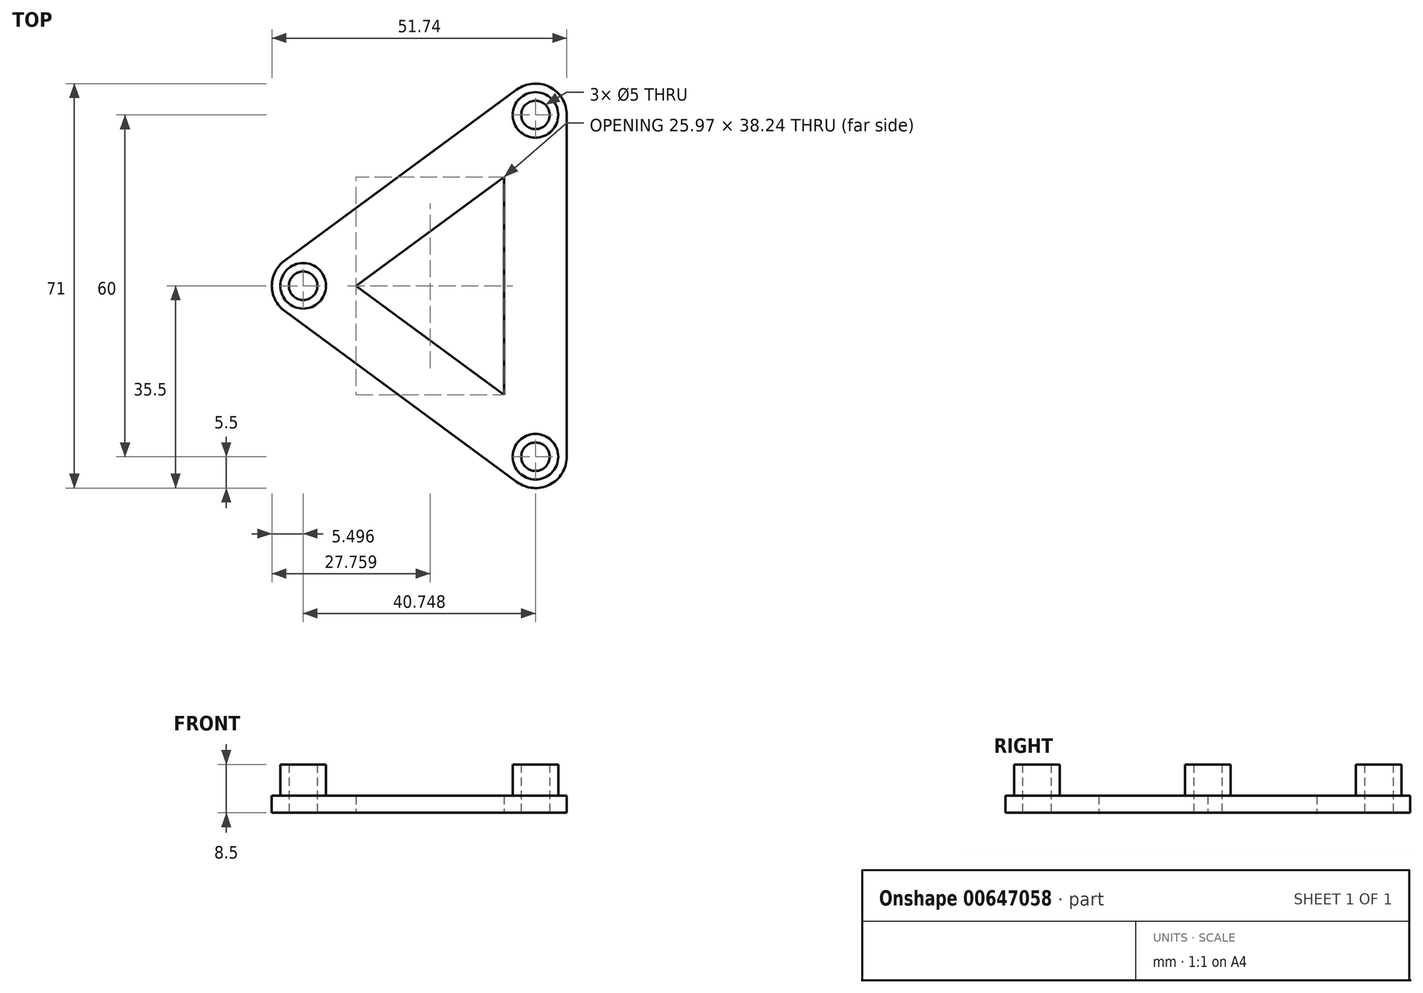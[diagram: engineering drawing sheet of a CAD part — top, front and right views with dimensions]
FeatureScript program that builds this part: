
annotation { "Feature Type Name" : "Feature", "Feature Type Description" : "" }
export const myFeature = defineFeature(function(context is Context, id is Id, definition is map)
    precondition{}
    {
        {
            var Q0;
            Q0=qCreatedBy(makeId("Top.planeOp"),FACE);
            var sketch = newSketch(context, id + "F0", { "sketchPlane" : qUnion([Q0])});
            skCircle(sketch, "E0", {"center": v(-17.31, 0) * mm, "radius": 2.5 * mm});
            skCircle(sketch, "E1", {"center": v(-17.31, 0) * mm, "radius": 5.5 * mm});
            skCircle(sketch, "E2", {"center": v(23.43, 30) * mm, "radius": 2.5 * mm});
            skCircle(sketch, "E3", {"center": v(23.43, 30) * mm, "radius": 5.5 * mm});
            skCircle(sketch, "E4", {"center": v(23.43, -30) * mm, "radius": 2.5 * mm});
            skCircle(sketch, "E5", {"center": v(23.43, -30) * mm, "radius": 5.5 * mm});
            skLineSegment(sketch, "E6", {"start": v(-17.31, 0) * mm, "end": v(23.43, 30) * mm, "construction": true});
            skLineSegment(sketch, "E7", {"start": v(-17.31, 0) * mm, "end": v(23.43, -30) * mm, "construction": true});
            skLineSegment(sketch, "E8", {"start": v(23.43, 30) * mm, "end": v(23.43, -30) * mm, "construction": true});
            skCircle(sketch, "E9", {"center": v(-17.31, 0) * mm, "radius": 4 * mm});
            skCircle(sketch, "E10", {"center": v(23.43, 30) * mm, "radius": 4 * mm});
            skCircle(sketch, "E11", {"center": v(23.43, -30) * mm, "radius": 4 * mm});
            skLineSegment(sketch, "E12.0", {"start": v(-8.04, 0) * mm, "end": v(17.93, 19.12) * mm});
            skLineSegment(sketch, "E12.1", {"start": v(-8.04, 0) * mm, "end": v(17.93, -19.12) * mm});
            skLineSegment(sketch, "E12.2", {"start": v(17.93, 19.12) * mm, "end": v(17.93, -19.12) * mm});
            skLineSegment(sketch, "E13.0", {"start": v(-20.57, 4.43) * mm, "end": v(20.17, 34.43) * mm});
            skLineSegment(sketch, "E13.1", {"start": v(-20.57, -4.43) * mm, "end": v(20.17, -34.43) * mm});
            skLineSegment(sketch, "E13.2", {"start": v(28.93, 30) * mm, "end": v(28.93, -30) * mm});
            skLineSegment(sketch, "E14", {"start": v(3.06, 15) * mm, "end": v(3.06, -15) * mm, "construction": true});
            skSolve(sketch);
        }
        {
            var Q0;
            Q0=makeQuery(id+"F0.imprint","IMPRINT",FACE,{"disambiguationData":[TD([[makeQuery(id+"F0.imprint","IMPRINT",EDGE,{"derivedFrom":sQuery(id+"F0.wireOp",EDGE,"E2")}),-1.0]])]});
            var Q1;
            {var subQ0=sQuery(id+"F0.wireOp",EDGE,"4292a800-b917-446e-8acb-4b11a4841fbd.0");var subQ1=sQuery(id+"F0.wireOp",EDGE,"E3");var subQ2=makeQuery(id+"F0.imprint","INTERSECT",VERTEX,{"derivedFrom":[subQ1,subQ0]});Q1=makeQuery(id+"F0.imprint","IMPRINT",FACE,{"disambiguationData":[TD([[makeQuery(id+"F0.imprint","IMPRINT",EDGE,{"disambiguationData":[TD([[subQ2,1.0]])],"derivedFrom":subQ1}),-1.0]])]});}
            var Q2;
            {var subQ0=sQuery(id+"F0.wireOp",EDGE,"b792d51c-0fe7-4bc2-b237-ce6525926208.0");Q2=makeQuery(id+"F0.imprint","IMPRINT",FACE,{"disambiguationData":[TD([[makeQuery(id+"F0.imprint","IMPRINT",EDGE,{"derivedFrom":subQ0}),-1.0]])]});}
            var Q3;
            Q3=makeQuery(id+"F0.imprint","IMPRINT",FACE,{"disambiguationData":[TD([[makeQuery(id+"F0.imprint","IMPRINT",EDGE,{"derivedFrom":sQuery(id+"F0.wireOp",EDGE,"E0")}),-1.0]])]});
            var Q4;
            {var subQ5=sQuery(id+"F0.wireOp",EDGE,"534e31a0-9855-4669-a3b1-e7b8400ff121.0");Q4=makeQuery(id+"F0.imprint","IMPRINT",FACE,{"disambiguationData":[TD([[makeQuery(id+"F0.imprint","IMPRINT",EDGE,{"derivedFrom":subQ5}),1.0]])]});}
            var Q5;
            {var subQ0=sQuery(id+"F0.wireOp",EDGE,"4292a800-b917-446e-8acb-4b11a4841fbd.0");var subQ1=sQuery(id+"F0.wireOp",EDGE,"E1");var subQ2=makeQuery(id+"F0.imprint","INTERSECT",VERTEX,{"derivedFrom":[subQ1,subQ0]});Q5=makeQuery(id+"F0.imprint","IMPRINT",FACE,{"disambiguationData":[TD([[makeQuery(id+"F0.imprint","IMPRINT",EDGE,{"disambiguationData":[TD([[subQ2,-1.0]])],"derivedFrom":subQ1}),-1.0]])]});}
            var Q6;
            {var subQ0=sQuery(id+"F0.wireOp",EDGE,"38d55559-1d0e-4463-9ff6-01328a6df294.0");var subQ1=sQuery(id+"F0.wireOp",EDGE,"E5");var subQ2=makeQuery(id+"F0.imprint","INTERSECT",VERTEX,{"derivedFrom":[subQ1,subQ0]});Q6=makeQuery(id+"F0.imprint","IMPRINT",FACE,{"disambiguationData":[TD([[makeQuery(id+"F0.imprint","IMPRINT",EDGE,{"disambiguationData":[TD([[subQ2,-1.0]])],"derivedFrom":subQ1}),-1.0]])]});}
            var Q7;
            Q7=makeQuery(id+"F0.imprint","IMPRINT",FACE,{"disambiguationData":[TD([[makeQuery(id+"F0.imprint","IMPRINT",EDGE,{"derivedFrom":sQuery(id+"F0.wireOp",EDGE,"E4")}),-1.0]])]});
            var Q8;
            {var subQ9=sQuery(id+"F0.wireOp",EDGE,"a9f5d0ef-61d3-43a7-a030-e22b1175c3c5.0");Q8=makeQuery(id+"F0.imprint","IMPRINT",FACE,{"disambiguationData":[TD([[makeQuery(id+"F0.imprint","IMPRINT",EDGE,{"derivedFrom":subQ9}),-1.0]])]});}
            var Q9;
            Q9=makeQuery(id+"F0.imprint","IMPRINT",FACE,{"disambiguationData":[TD([[makeQuery(id+"F0.imprint","IMPRINT",EDGE,{"derivedFrom":sQuery(id+"F0.wireOp",EDGE,"E11")}),-1.0]])]});
            var Q10;
            Q10=makeQuery(id+"F0.imprint","IMPRINT",FACE,{"disambiguationData":[TD([[makeQuery(id+"F0.imprint","IMPRINT",EDGE,{"derivedFrom":sQuery(id+"F0.wireOp",EDGE,"E9")}),-1.0]])]});
            var Q11;
            Q11=makeQuery(id+"F0.imprint","IMPRINT",FACE,{"disambiguationData":[TD([[makeQuery(id+"F0.imprint","IMPRINT",EDGE,{"derivedFrom":sQuery(id+"F0.wireOp",EDGE,"E10")}),-1.0]])]});
            extrude(context, id + "F1", {"entities" : qUnion([Q0, Q1, Q2, Q3, Q4, Q5, Q6, Q7, Q8, Q9, Q10, Q11]), "depth" : 3 * mm, "offsetDistance" : 25 * mm});
        }
        {
            var Q0;
            Q0=makeQuery(id+"F0.imprint","IMPRINT",FACE,{"disambiguationData":[TD([[makeQuery(id+"F0.imprint","IMPRINT",EDGE,{"derivedFrom":sQuery(id+"F0.wireOp",EDGE,"E2")}),-1.0]])]});
            var Q1;
            Q1=makeQuery(id+"F0.imprint","IMPRINT",FACE,{"disambiguationData":[TD([[makeQuery(id+"F0.imprint","IMPRINT",EDGE,{"derivedFrom":sQuery(id+"F0.wireOp",EDGE,"E0")}),-1.0]])]});
            var Q2;
            Q2=makeQuery(id+"F0.imprint","IMPRINT",FACE,{"disambiguationData":[TD([[makeQuery(id+"F0.imprint","IMPRINT",EDGE,{"derivedFrom":sQuery(id+"F0.wireOp",EDGE,"E4")}),-1.0]])]});
            extrude(context, id + "F2", {"entities" : qUnion([Q0, Q1, Q2]), "operationType" : NewBodyOperationType.ADD, "depth" : 8.5 * mm, "offsetDistance" : 25 * mm});
        }
    });
